# Revit family: Hager TPN DB (with door) v2
name_source: partatom
category: Electrical Equipment
revit_build: Autodesk Revit 2013 (Build: 20120221_2030(x64)
units: mm (PartAtom-declared; Revit-internal decimal feet)

## types (44) — shared parameters
CE Approval = Yes
Colour = BS4800:2011 00A01 Oyster Grey
Door = 46 mm  [stored 0.150919 ft]
Enclosure Rating = IP3X
Frequency = 50 Hz
Location = Indoors
Location of Manufacturer = Telford, TF1 7FT
MCB Rating = 63 A
Mains Type = 3 phase
Manufacturer = Hager UK Ltd
Manufacturer Website = www.hager.co.uk
Neutral Rating = 100.00%
Number of Poles = 3
Overall Width = 465 mm  [stored 1.52559 ft]
Packaging Recyclable = Yes
Packaging Weight = 1.00 kg
Pollution Degree = 2
Product Range = Invicta 3 TPN DB Type B
Reference Standard = BS EN 61439-3
Revision = 3
Supply Phase = 1,3
URL = www.hager.co.uk
Ui Rating = 690 V
Uimp Rating = 4000 V
Voltage = 415
Warranty ID = 24 Months

## per-type parameters (varying)
| type | Busbar Rating | Default Elevation | Description | Door Type | EAN | Hager Catalogue Ref | Max #3 Pole Breakers | Model | Outging Ways (TP) | Overall Height | Product Description | Product Literature | Product Weight |
| TPN DB 125A 04 Way GD | 125 A | 1200 mm | JK1 TPN B Board 4x 63A TP Ways DB Glazed Door | Single Glazed Door | 5015652250234 | JK104BG | 4 | JK104BG | 4 | 133 mm  [stored 0.436352 ft] | JK1 TPN B Board 4x 63A TP Ways DB Glazed Door | www.hager.co.uk/?artnr=JK104BG | 8.80 kg |
| TPN DB 125A 06 Way GD | 125 A | 1200 mm | JK1 TPN B Board 6x 63A TP Ways DB Glazed Door | Single Glazed Door | 5015652250265 | JK106BG | 6 | JK106BG | 6 | 133 mm  [stored 0.436352 ft] | JK1 TPN B Board 6x 63A TP Ways DB Glazed Door | www.hager.co.uk/?artnr=JK106BG | 9.60 kg |
| TPN DB 125A 08 Way GD | 125 A | 1200 mm | JK1 TPN B Board 8x 63A TP Ways DB Glazed Door | Single Glazed Door | 5015652250289 | JK108BG | 8 | JK108BG | 8 | 133 mm  [stored 0.436352 ft] | JK1 TPN B Board 8x 63A TP Ways DB Glazed Door | www.hager.co.uk/?artnr=JK108BG | 10.50 kg |
| TPN DB 125A 12 Way GD | 125 A | 1200 mm | JK1 TPN B Board 12x 63A TP Ways DB Glazed Door | Single Glazed Door | 5015652250357 | JK112BG | 12 | JK112BG | 12 | 133 mm  [stored 0.436352 ft] | JK1 TPN B Board 12x 63A TP Ways DB Glazed Door | www.hager.co.uk/?artnr=JK112BG | 14.00 kg |
| TPN DB 125A 18 Way GD | 125 A | 1200 mm | JK1 TPN B Board 18x 63A TP Ways DB Glazed Door | Single Glazed Door | 5015652276807 | JK118BG | 18 | JK118BG | 18 | 133 mm  [stored 0.436352 ft] | JK1 TPN B Board 18x 63A TP Ways DB Glazed Door | www.hager.co.uk/?artnr=JK118BG | 18.50 kg |
| TPN DB 125A 24 Way GD | 125 A | 800 mm | JK1 TPN B Board 24x 63A TP Ways DB Glazed Door | Single Glazed Door | 5015652276821 | JK124BG | 24 | JK124BG | 24 | 133 mm  [stored 0.436352 ft] | JK1 TPN B Board 24x 63A TP Ways DB Glazed Door | www.hager.co.uk/?artnr=JK124BG | 20.00 kg |
| TPN DB 125A 16 Way GD | 125 A | 1200 mm | JK1 TPN B Board 16x 63A TP Ways DB Glazed Door | Single Glazed Door | 5015652250371 | JK116BG | 16 | JK116BG | 16 | 133 mm  [stored 0.436352 ft] | JK1 TPN B Board 16x 63A TP Ways DB Glazed Door | www.hager.co.uk/?artnr=JK116BG | 17.50 kg |
| TPB DB 125A 04 Way PD | 125 A | 1200 mm | JK1 TPN B Board 4x 63A TP Ways DB Plain Door | Single Plain Door | 5015652250227 | JK104B | 4 | JK104B | 4 | 133 mm  [stored 0.436352 ft] | JK1 TPN B Board 4x 63A TP Ways DB Plain Door | www.hager.co.uk/?artnr=JK104B | 8.80 kg |
| TPN DB 125A 06 Way PD | 125 A | 1200 mm | JK1 TPN B Board 6x 63A TP Ways DB Plain Door | Single Plain Door | 5015652250258 | JK106B | 6 | JK106B | 6 | 133 mm  [stored 0.436352 ft] | JK1 TPN B Board 6x 63A TP Ways DB Plain Door | www.hager.co.uk/?artnr=JK106B | 9.60 kg |
| TPN DB 125A 08 Way PD | 125 A | 1200 mm | JK1 TPN B Board 8x 63A TP Ways DB Plain Door | Single Plain Door | 5015652250272 | JK108B | 8 | JK108B | 8 | 133 mm  [stored 0.436352 ft] | JK1 TPN B Board 8x 63A TP Ways DB Plain Door | www.hager.co.uk/?artnr=JK108B | 10.50 kg |
| TPN DB 125A 12 Way PD | 125 A | 1200 mm | JK1 TPN B Board 12x 63A TP Ways DB Plain Door | Single Plain Door | 5015652250340 | JK112B | 12 | JK112B | 12 | 133 mm  [stored 0.436352 ft] | JK1 TPN B Board 12x 63A TP Ways DB Plain Door | www.hager.co.uk/?artnr=JK112B | 14.00 kg |
| TPN DB 125A 18 Way PD | 125 A | 1200 mm | JK1 TPN B Board 18x 63A TP Ways DB Plain Door | Single Plain Door | 5015652276814 | JK118B | 18 | JK118B | 18 | 133 mm  [stored 0.436352 ft] | JK1 TPN B Board 18x 63A TP Ways DB Plain Door | www.hager.co.uk/?artnr=JK118B | 18.50 kg |
| TPN DB 125A 24 Way PD | 125 A | 800 mm | JK1 TPN B Board 24x 63A TP Ways DB Plain Door | Single Plain Door | 5015652276838 | JK124B | 24 | JK124B | 24 | 133 mm  [stored 0.436352 ft] | JK1 TPN B Board 24x 63A TP Ways DB Plain Door | www.hager.co.uk/?artnr=JK124B | 20.00 kg |
| TPN DB 125A 16 Way PD | 125 A | 1200 mm | JK1 TPN B Board 16x 63A TP Ways DB Plain Door | Single Plain Door | 5015652250364 | JK116B | 16 | JK116B | 16 | 133 mm  [stored 0.436352 ft] | JK1 TPN B Board 16x 63A TP Ways DB Plain Door | www.hager.co.uk/?artnr=JK116B | 17.50 kg |
| TPN DB 250A 08 Way GD | 250 A | 1200 mm | JK2 TPN B Board 8x 63A TP Ways DB Glazed Door | Single Glazed Door | 5015652250395 | JK208BG | 8 | JK208BG | 8 | 166 mm | JK2 TPN B Board 8x 63A TP Ways DB Glazed Door | www.hager.co.uk/?artnr=JK208BG | 12.60 kg |
| TPN DB 250A 12 Way GD | 250 A | 1200 mm | JK2 TPN B Board 12x 63A TP Ways DB Glazed Door | Single Glazed Door | 5015652250449 | JK212BG | 12 | JK212BG | 12 | 166 mm | JK2 TPN B Board 12x 63A TP Ways DB Glazed Door | www.hager.co.uk/?artnr=JK212BG | 16.00 kg |
| TPN DB 250A 18 Way GD | 250 A | 1200 mm | JK2 TPN B Board 18x 63A TP Ways DB Glazed Door | Single Glazed Door | 5015652250487 | JK218BG | 18 | JK218BG | 18 | 166 mm | JK2 TPN B Board 18x 63A TP Ways DB Glazed Door | www.hager.co.uk/?artnr=JK218BG | 23.30 kg |
| TPN DB 250A 24 Way GD | 250 A | 800 mm | JK2 TPN B Board 24x 63A TP Ways DB Glazed Door | Single Glazed Door | 5015652250500 | JK224BG | 24 | JK224BG | 24 | 166 mm | JK2 TPN B Board 24x 63A TP Ways DB Glazed Door | www.hager.co.uk/?artnr=JK224BG | 26.20 kg |
| TPN DB 250A 08 Way PD | 250 A | 1200 mm | JK2 TPN B Board 8x 63A TP Ways DB Plain Door | Single Plain Door | 5015652250388 | JK208B | 8 | JK208B | 8 | 166 mm | JK2 TPN B Board 8x 63A TP Ways DB Plain Door | www.hager.co.uk/?artnr=JK208B | 12.60 kg |
| TPN DB 250A 12 Way PD | 250 A | 1200 mm | JK2 TPN B Board 12x 63A TP Ways DB Plain Door | Single Plain Door | 5015652250432 | JK212B | 12 | JK212B | 12 | 166 mm | JK2 TPN B Board 12x 63A TP Ways DB Plain Door | www.hager.co.uk/?artnr=JK212B | 16.00 kg |
| TPN DB 250A 18 Way PD | 250 A | 1200 mm | JK2 TPN B Board 18x 63A TP Ways DB Plain Door | Single Plain Door | 5015652250470 | JK218B | 18 | JK218B | 18 | 166 mm | JK2 TPN B Board 18x 63A TP Ways DB Plain Door | www.hager.co.uk/?artnr=JK218B | 23.30 kg |
| TPN DB 250A 24 Way PD | 250 A | 800 mm | JK2 TPN B Board 24x 63A TP Ways DB Plain Door | Single Plain Door | 5015652250494 | JK224B | 24 | JK224B | 24 | 166 mm | JK2 TPN B Board 24x 63A TP Ways DB Plain Door | www.hager.co.uk/?artnr=JK224B | 26.20 kg |
| TPN DB 250A 16 Way GD | 250 A | 1200 mm | JK2 TPN B Board 16x 63A TP Ways DB Glazed Door | Single Glazed Door | 5015652250463 | JK216BG | 16 | JK216BG | 16 | 166 mm | JK2 TPN B Board 16x 63A TP Ways DB Glazed Door | www.hager.co.uk/?artnr=JK216BG | 20.40 kg |
| TPN DB 250A 16 Way PD | 250 A | 1200 mm | JK2 TPN B Board 16x 63A TP Ways DB Plain Door | Single Plain Door | 5015652250456 | JK216B | 16 | JK216B | 16 | 166 mm | JK2 TPN B Board 16x 63A TP Ways DB Plain Door | www.hager.co.uk/?artnr=JK216B | 20.40 kg |
| TPN DB 125A 10 Way GD Metered Pulsed (Power&Lighting 4+6W) | 125 A | 1200 mm | JK1 TPN B Board 10x 63A TP (4+6) Ways DB Glazed Door Metered (Pulsed) | Single Glazed Door | 5015654758912 | JK146B | 10 | JK146B | 10 | 166 mm | JK1 TPN B Board 10x 63A TP (4+6) Ways DB Glazed Door Metered (Pulsed) | www.hager.co.uk/?artnr=JK146B | 25.00 kg |
| TPN DB 125A 10 Way GD Metered Modbus (Power&Lighting 4+6W) | 125 A | 1200 mm | JK1 TPN B Board 10x 63A TP (4+6) Ways DB Glazed Door Metered (Modbus) | Single Glazed Door | 5015654758929 | JK146BM | 10 | JK146BM | 10 | 166 mm | JK1 TPN B Board 10x 63A TP (4+6) Ways DB Glazed Door Metered (Modbus) | www.hager.co.uk/?artnr=JK146BM | 25.00 kg |
| TPN DB 125A 14 Way GD Metered Pulsed (Power&Lighting 6+8W) | 125 A | 1200 mm | JK1 TPN B Board 10x 63A TP (6+8) Ways DB Glazed Door Metered (Pulsed) | Single Glazed Door | 5015654758936 | JK168B | 14 | JK168B | 14 | 166 mm | JK1 TPN B Board 10x 63A TP (6+8) Ways DB Glazed Door Metered (Pulsed) | www.hager.co.uk/?artnr=JK168B | 25.00 kg |
| TPN DB 125A 14 Way GD Metered Modbus (Power&Lighting 6+8W) | 125 A | 1200 mm | JK1 TPN B Board 10x 63A TP (6+8) Ways DB Glazed Door Metered (Modbus) | Single Glazed Door | 5015654758943 | JK168BM | 14 | JK168BM | 14 | 166 mm | JK1 TPN B Board 10x 63A TP (6+8) Ways DB Glazed Door Metered (Modbus) | www.hager.co.uk/?artnr=JK168BM | 25.00 kg |
| TPN DB 125A 20 Way GD Metered Pulsed (Power&Lighting 4+16W) | 125 A | 1200 mm | JK1 TPN B Board 10x 63A TP (4+16) Ways DB Glazed Door Metered (Pulsed) | Single Glazed Door | 5015652252498 | JK1416B | 20 | JK1416B | 20 | 166 mm | JK1 TPN B Board 10x 63A TP (4+16) Ways DB Glazed Door Metered (Pulsed) | www.hager.co.uk/?artnr=JKD1416B | 25.00 kg |
| TPN DB 125A 20 Way GD Metered Modbus (Power&Lighting 4+16W) | 125 A | 1200 mm | JK1 TPN B Board 10x 63A TP (4+16) Ways DB Glazed Door Metered (Modbus) | Single Glazed Door | 5015654758899 | JK1416BM | 20 | JK1416BM | 20 | 166 mm | JK1 TPN B Board 10x 63A TP (4+16) Ways DB Glazed Door Metered (Modbus) | www.hager.co.uk/?artnr=JKD1416BM | 25.00 kg |
| TPN DB 125A 20 Way GD Metered Pulsed (Power&Lighting 8+12W) | 125 A | 1200 mm | JK1 TPN B Board 10x 63A TP (8+12) Ways DB Glazed Door Metered (Pulsed) | Single Glazed Door | 5015652252504 | JK1812B | 20 | JK1812B | 20 | 166 mm | JK1 TPN B Board 10x 63A TP (8+12) Ways DB Glazed Door Metered (Pulsed) | www.hager.co.uk/?artnr=JKD1812B | 25.00 kg |
| TPN DB 125A 20 Way GD Metered Modbus (Power&Lighting 8+12W) | 125 A | 1200 mm | JK1 TPN B Board 10x 63A TP (8+12) Ways DB Glazed Door Metered (Modbus) | Single Glazed Door | 5015654758905 | JK1812BM | 20 | JK1812BM | 20 | 166 mm | JK1 TPN B Board 10x 63A TP (8+12) Ways DB Glazed Door Metered (Modbus) | www.hager.co.uk/?artnr=JKD1812BM | 25.00 kg |
| TPN DB 125A 10 Way GD Metered Pluggable (Power&Lighting 4+6W) | 125 A | 1200 mm | JK1 TPN B Board 10x 63A TP (4+6) Ways DB Glazed Door Metered (Pluggable) | Single Glazed Door | 3250610459546 | JK146PM | 10 | JK146PM | 10 | 166 mm | JK1 TPN B Board 10x 63A TP (4+6) Ways DB Glazed Door Metered (Pluggable) | www.hager.co.uk/?artnr=JK146PM | 21.00 kg |
| TPN DB 125A 10 Way GD Metered Pluggable (Power&Lighting 6+4W) | 125 A | 1200 mm | JK1 TPN B Board 10x 63A TP (6+4) Ways DB Glazed Door Metered (Pluggable) | Single Glazed Door | 5015652600244 | JK164PM | 10 | JK164PM | 10 | 166 mm | JK1 TPN B Board 10x 63A TP (6+4) Ways DB Glazed Door Metered (Pluggable) | www.hager.co.uk/?artnr=JK164PM | 21.00 kg |
| TPN DB 125A 12 Way GD Metered Pluggable (Power&Lighting 6+6W) | 125 A | 1200 mm | JK1 TPN B Board 12x 63A TP (6+6) Ways DB Glazed Door Metered (Pluggable) | Single Glazed Door | 5015652600251 | JK166PM | 12 | JK166PM | 12 | 166 mm | JK1 TPN B Board 12x 63A TP (6+6) Ways DB Glazed Door Metered (Pluggable) | www.hager.co.uk/?artnr=JK166PM | 21.50 kg |
| TPN DB 125A 14 Way GD Metered Pluggable (Power&Lighting 6+8W) | 125 A | 1200 mm | JK1 TPN B Board 10x 63A TP (6+8) Ways DB Glazed Door Metered (Pluggable) | Single Glazed Door | 3250610459553 | JK168PM | 14 | JK168PM | 14 | 166 mm | JK1 TPN B Board 10x 63A TP (6+8) Ways DB Glazed Door Metered (Pluggable) | www.hager.co.uk/?artnr=JK168PM | 23.00 kg |
| TPN DB 125A 14 Way GD Metered Pluggable (Power&Lighting 8+6W) | 125 A | 1200 mm | JK1 TPN B Board 10x 63A TP (8+6) Ways DB Glazed Door Metered (Pluggable) | Single Glazed Door | 5015652600268 | JK186PM | 14 | JK186PM | 14 | 166 mm | JK1 TPN B Board 10x 63A TP (8+6) Ways DB Glazed Door Metered (Pluggable) | www.hager.co.uk/?artnr=JK186PM | 23.00 kg |
| TPN DB 125A 16 Way GD Metered Pluggable (Power&Lighting 8+8W) | 125 A | 1200 mm | JK1 TPN B Board 12x 63A TP (8+8) Ways DB Glazed Door Metered (Pluggable) | Single Glazed Door | 5015652600275 | JK188PM | 16 | JK188PM | 16 | 166 mm | JK1 TPN B Board 12x 63A TP (8+8) Ways DB Glazed Door Metered (Pluggable) | www.hager.co.uk/?artnr=JK188PM | 23.50 kg |
| TPN DB 125A 20 Way GD Metered Pluggable (Power&Lighting 4+16W) | 125 A | 1200 mm | JK1 TPN B Board 20x 63A TP (4+16) Ways DB Glazed Door Metered (Pluggable) | Single Glazed Door | 3250610459539 | JK1416PM | 20 | JK1416PM | 20 | 166 mm | JK1 TPN B Board 20x 63A TP (4+16) Ways DB Glazed Door Metered (Pluggable) | www.hager.co.uk/?artnr=JK1416PM | 25.00 kg |
| TPN DB 125A 20 Way GD Metered Pluggable (Power&Lighting 16+4W) | 125 A | 1200 mm | JK1 TPN B Board 20x 63A TP (16+4) Ways DB Glazed Door Metered (Pluggable) | Single Glazed Door | 5015652600220 | JK1164PM | 20 | JK1164PM | 20 | 166 mm | JK1 TPN B Board 20x 63A TP (16+4) Ways DB Glazed Door Metered (Pluggable) | www.hager.co.uk/?artnr=JK1164PM | 25.00 kg |
| TPN DB 125A 20 Way GD Metered Pluggable (Power&Lighting 8+12W) | 125 A | 1200 mm | JK1 TPN B Board 20x 63A TP (8+12) Ways DB Glazed Door Metered (Pluggable) | Single Glazed Door | 3250610459560 | JK1812PM | 20 | JK1812PM | 20 | 166 mm | JK1 TPN B Board 20x 63A TP (8+12) Ways DB Glazed Door Metered (Pluggable) | www.hager.co.uk/?artnr=JK1812PM | 25.00 kg |
| TPN DB 125A 20 Way GD Metered Pluggable (Power&Lighting 12+8W) | 125 A | 1200 mm | JK1 TPN B Board 20x 63A TP (12+8) Ways DB Glazed Door Metered (Pluggable) | Single Glazed Door | 5015652600213 | JK1128PM | 20 | JK1128PM | 20 | 166 mm | JK1 TPN B Board 20x 63A TP (12+8) Ways DB Glazed Door Metered (Pluggable) | www.hager.co.uk/?artnr=JK1128PM | 25.00 kg |
| TPN DB 125A 24 Way GD Metered Pluggable (Power&Lighting 12+12W) | 125 A | 1200 mm | JK1 TPN B Board 24x 63A TP (12+12) Ways DB Glazed Door Metered (Pluggable) | Single Glazed Door | 5015652600206 | JK11212PM | 24 | JK11212PM | 24 | 166 mm | JK1 TPN B Board 24x 63A TP (12+12) Ways DB Glazed Door Metered (Pluggable) | www.hager.co.uk/?artnr=JK11212PM | 25.00 kg |
| TPN DB 125A 20 Way GD Metered Pluggable (Power&Lighting 8+8+4W) | 125 A | 1200 mm | JK2 TPN B Board 20x 63A TP (8+8+4) Ways DB Glazed Door Metered (Pluggable) | Double Glazed Door | 5015652600299 | JK2884PM | 20 | JK2884PM | 20 | 166 mm | JK2 TPN B Board 20x 63A TP (8+8+4) Ways DB Glazed Door Metered (Pluggable) | www.hager.co.uk/?artnr=JK2884PM | 28.00 kg |

note: [stored X ft] marks values corroborated as IEEE doubles in the binary element streams (Revit-internal decimal feet)

## geometry (parser evidence)
native form markers: Sweep x2
no freeform markers — native parametric forms only
